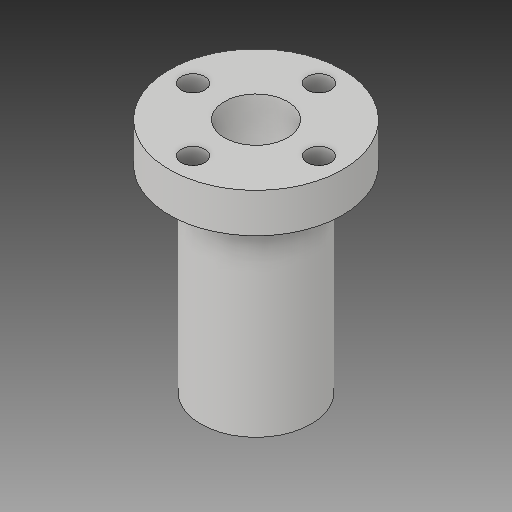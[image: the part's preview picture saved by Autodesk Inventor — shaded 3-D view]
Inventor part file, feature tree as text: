
AUTODESK INVENTOR PART (.ipt)
format: ipt  version: 2019 (Build 230136000, 136)  size: 135,680 bytes
history: native  units: in
note: dims shown in document units (in); Inventor stores cm internally (conversion verified against a paired STEP export)
features: sketch x2, other x2, revolve x1, extrude x1, plane x1
ambient origin geometry x8: Origin, YZ Plane, XZ Plane, XY Plane, X Axis, Y Axis, Z Axis, Center Point
bodies: Solid1 (feature_tree)
feature tree (7):
  revolve  "Revolution1"  [1 undecoded]
  extrude  "Extrusion1"  Depth=0.1575in
  plane  "Work Plane1"
  sketch  "Sketch1"  dims[d1=0.1575in d2=0.4331in]
  sketch  "Sketch2"  dims[d3=0.1969in d4=0.1575in d5=0.9843in d6=90.0deg d7=0.315in d8=0.1181in d9=1.5748in d11=360.0deg d13=1.0in d14=0.0in]
  other  "Work Axis1"
  other  "Work Axis2"
note: 1 required parameter value undecoded (feature->parameter linkage not recoverable at this tier; creation-order binding heuristic only, values carry confidence <= 0.55)
